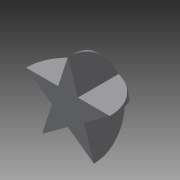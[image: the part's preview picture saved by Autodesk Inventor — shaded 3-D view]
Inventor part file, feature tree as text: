
AUTODESK INVENTOR PART (.ipt)
format: ipt  version: 2013 (Build 170138000, 138)  size: 98,816 bytes
history: native  units: mm
features: sketch x2, other x1, revolve x1, extrude x1
ambient origin geometry x8: Origin, YZ Plane, XZ Plane, XY Plane, X Axis, Y Axis, Z Axis, Center Point
feature tree (5):
  other  "ソリッド1"
  revolve  "回転1"
  extrude  "押し出し1"  Depth=10.0mm
  sketch  "スケッチ1"
  sketch  "スケッチ2"
